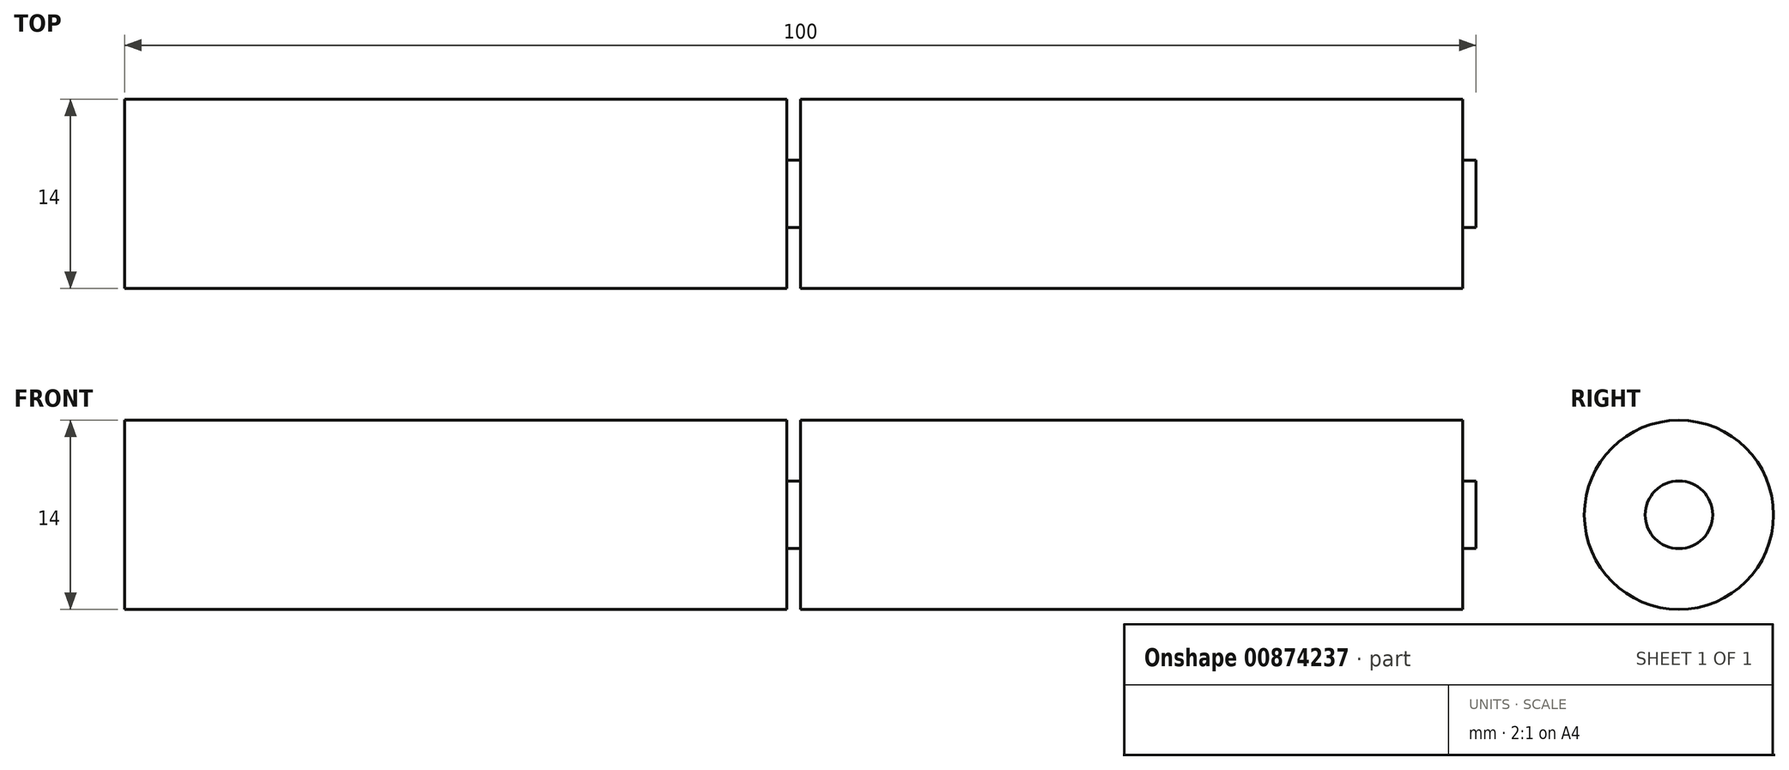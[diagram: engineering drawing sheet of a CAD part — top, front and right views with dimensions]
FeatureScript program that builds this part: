
annotation { "Feature Type Name" : "Feature", "Feature Type Description" : "" }
export const myFeature = defineFeature(function(context is Context, id is Id, definition is map)
    precondition{}
    {
        {
            assignVariable(context, id + "F0", {"name" : "cell_length", "anyValue" : 50});
        }
        {
            assignVariable(context, id + "F1", {"name" : "button_height", "anyValue" : 1});
        }
        {
            var Q0;
            Q0=qCreatedBy(makeId("Front.planeOp"),FACE);
            var sketch = newSketch(context, id + "F2", { "sketchPlane" : qUnion([Q0])});
            skLineSegment(sketch, "E0.bottom", {"start": v(-24.5, 0) * mm, "end": v(24.5, 0) * mm});
            skLineSegment(sketch, "E0.top", {"start": v(-24.5, 7) * mm, "end": v(24.5, 7) * mm});
            skLineSegment(sketch, "E0.left", {"start": v(-24.5, 0) * mm, "end": v(-24.5, 7) * mm});
            skLineSegment(sketch, "E0.right", {"start": v(24.5, 0) * mm, "end": v(24.5, 7) * mm});
            skLineSegment(sketch, "E1.bottom", {"start": v(24.5, 0) * mm, "end": v(25.5, 0) * mm});
            skLineSegment(sketch, "E1.top", {"start": v(24.5, 2.5) * mm, "end": v(25.5, 2.5) * mm});
            skLineSegment(sketch, "E1.left", {"start": v(24.5, 0) * mm, "end": v(24.5, 2.5) * mm});
            skLineSegment(sketch, "E1.right", {"start": v(25.5, 0) * mm, "end": v(25.5, 2.5) * mm});
            skSolve(sketch);
        }
        {
            var Q0;
            Q0=makeQuery(id+"F2.imprint","IMPRINT",FACE,{"disambiguationData":[TD([[makeQuery(id+"F2.imprint","IMPRINT",EDGE,{"derivedFrom":sQuery(id+"F2.wireOp",EDGE,"E0.bottom")}),1.0]])]});
            var Q1;
            Q1=makeQuery(id+"F2.imprint","IMPRINT",FACE,{"disambiguationData":[TD([[makeQuery(id+"F2.imprint","IMPRINT",EDGE,{"derivedFrom":sQuery(id+"F2.wireOp",EDGE,"E1.bottom")}),1.0]])]});
            var Q2;
            Q2=sQuery(id+"F2.wireOp",EDGE,"E0.bottom");
            revolve(context, id + "F3", {"surfaceOperationType" : NewSurfaceOperationType.NEW, "entities" : qUnion([Q0, Q1]), "axis" : qUnion([Q2]), "revolveType" : RevolveType.FULL});
        }
        {
            var Q0;
            Q0=makeQuery(id+"F3.opRevolve","SWEPT_BODY",BODY,{"disambiguationData":[OSD([sQuery(id+"F2.wireOp",EDGE,"E0.bottom"),sQuery(id+"F2.wireOp",EDGE,"E0.top"),sQuery(id+"F2.wireOp",EDGE,"E0.left"),sQuery(id+"F2.wireOp",EDGE,"E0.right"),sQuery(id+"F2.wireOp",EDGE,"E1.bottom"),sQuery(id+"F2.wireOp",EDGE,"E1.top"),sQuery(id+"F2.wireOp",EDGE,"E1.right")])]});
            transform(context, id + "F4", {"entities" : qUnion([Q0]), "transformType" : TransformType.TRANSLATION_3D, "dx" : (-getVariable(context, 'cell_length') / 2 - getVariable(context, 'button_height') / 2) * mm, "dy" : 0 * mm, "dz" : 0 * mm, "makeCopy" : false});
        }
        {
            var Q0;
            Q0=makeQuery(id+"F3.opRevolve","SWEPT_BODY",BODY,{"disambiguationData":[OSD([sQuery(id+"F2.wireOp",EDGE,"E0.bottom"),sQuery(id+"F2.wireOp",EDGE,"E0.top"),sQuery(id+"F2.wireOp",EDGE,"E0.left"),sQuery(id+"F2.wireOp",EDGE,"E0.right"),sQuery(id+"F2.wireOp",EDGE,"E1.bottom"),sQuery(id+"F2.wireOp",EDGE,"E1.top"),sQuery(id+"F2.wireOp",EDGE,"E1.right")])]});
            transform(context, id + "F5", {"entities" : qUnion([Q0]), "transformType" : TransformType.COPY});
        }
        {
            var Q0;
            Q0=makeQuery(id+"F5.opPattern","COPY",BODY,{"derivedFrom":makeQuery(id+"F3.opRevolve","SWEPT_BODY",BODY,{"disambiguationData":[OSD([sQuery(id+"F2.wireOp",EDGE,"E0.bottom"),sQuery(id+"F2.wireOp",EDGE,"E0.top"),sQuery(id+"F2.wireOp",EDGE,"E0.left"),sQuery(id+"F2.wireOp",EDGE,"E0.right"),sQuery(id+"F2.wireOp",EDGE,"E1.bottom"),sQuery(id+"F2.wireOp",EDGE,"E1.top"),sQuery(id+"F2.wireOp",EDGE,"E1.right")])]}),"instanceName":"1"});
            transform(context, id + "F6", {"entities" : qUnion([Q0]), "transformType" : TransformType.TRANSLATION_3D, "dx" : (getVariable(context, 'cell_length')) * mm, "dy" : 0 * mm, "dz" : 0 * mm, "makeCopy" : false});
        }
    });
